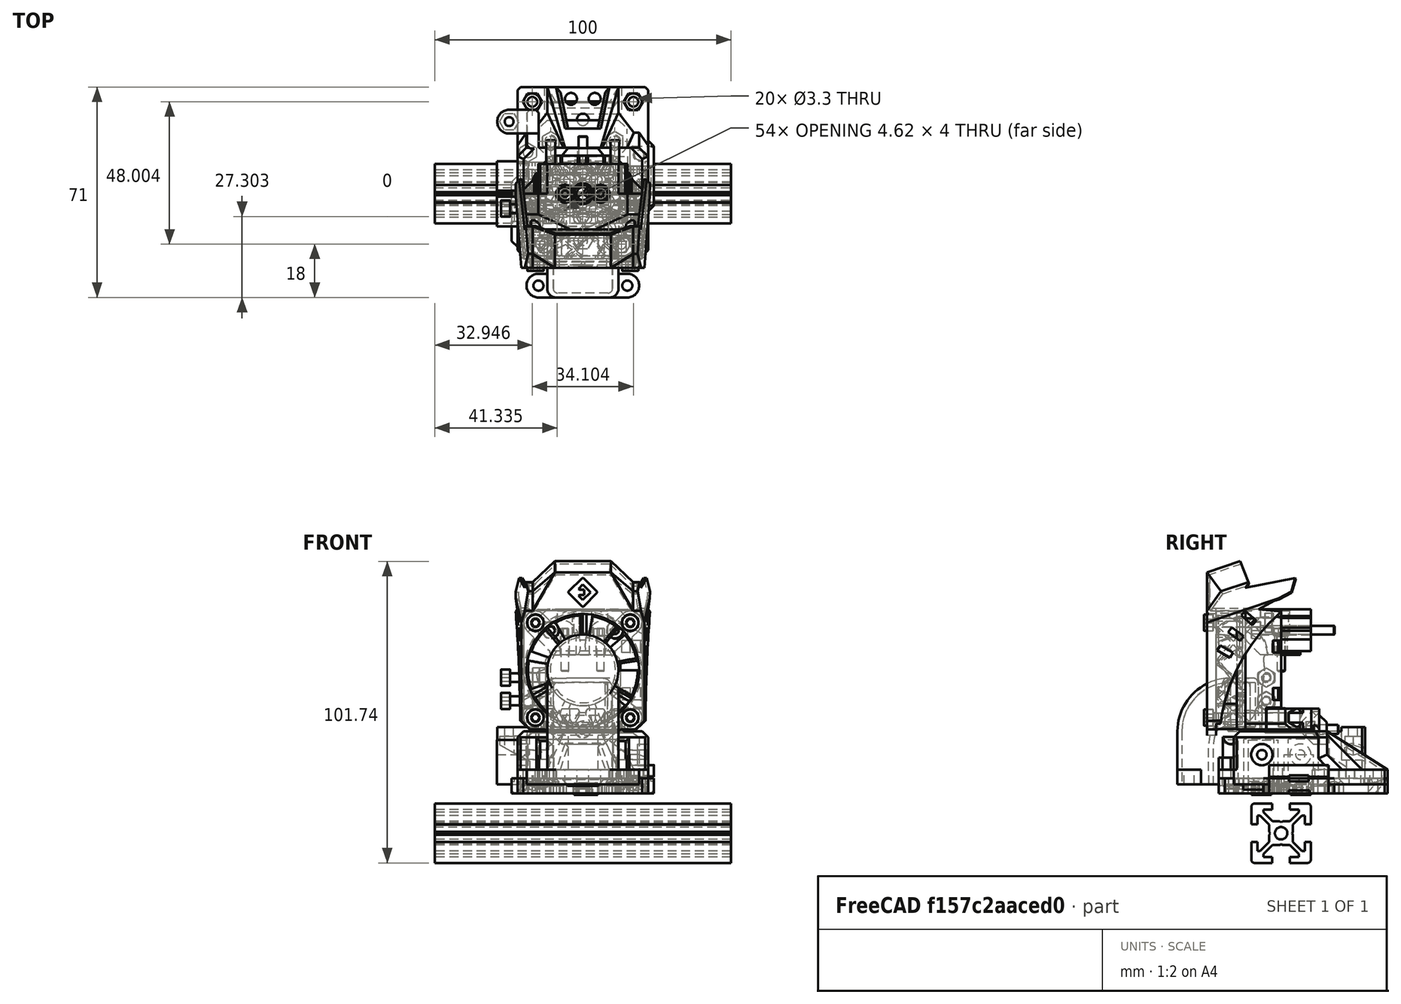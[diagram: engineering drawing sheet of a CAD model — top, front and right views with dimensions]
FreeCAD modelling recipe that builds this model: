
FCSTD DOCUMENT  (FreeCAD 0.19R24291 (Git))
Label: face-plate
License: Other
LicenseURL: GPL3
objects: Part::Feature×62, Part::MultiFuse×19, Part::Box×18, Part::Cylinder×16, Part::Cut×14, Part::Chamfer×6, Part::Refine×3, Part::Fillet×3, App::Part×2, Part::Extrusion×1, Part::MultiCommon×1
note: 143 computed .brp shape members not serialized (recipe doc carries the construction recipe); baked Part::Feature solids carry a one-line shape summary decoded from their .brp

FEATURE [Part::Cylinder] Cylinder
  Angle = 360
  AttacherType = Attacher::AttachEngine3D
  Height = 10
  Placement = pos=(-10.8,17.71,0) rot=(0,0,1;1.5708rad)
  Radius = 2
FEATURE [Part::Cylinder] Cylinder001
  Angle = 360
  AttacherType = Attacher::AttachEngine3D
  Height = 10
  Placement = pos=(10.8,17.705,0) rot=(0,0,1;0rad)
  Radius = 2
FEATURE [Part::MultiFuse] Fusion002
  Shapes = -> [Cylinder001,Cylinder]
FEATURE [Part::Feature] Extrude003002001  label="2020"
  Placement = pos=(50,0,-13) rot=(0,-1,0;1.5708rad)
  shape: bbox 100 x 20 x 20 mm, 63 faces (baked)
FEATURE [Part::Box] Box004  label="Cube004"
  AttacherType = Attacher::AttachEngine3D
  Height = 10.39
  Length = 2.5
  Placement = pos=(12.5,2.75,0) rot=(0,0,1;0rad)
  Width = 6.5
FEATURE [Part::Box] Box005  label="Cube005"
  AttacherType = Attacher::AttachEngine3D
  Height = 10.39
  Length = 2.5
  Placement = pos=(-15,-9.25,0) rot=(0,0,1;0rad)
  Width = 6.5
FEATURE [Part::Box] Box006  label="Cube006"
  AttacherType = Attacher::AttachEngine3D
  Height = 2.5
  Length = 10
  Placement = pos=(-37,-9.5,-1) rot=(0,0,1;0rad)
  Width = 7
FEATURE [Part::Box] Box007  label="Cube007"
  AttacherType = Attacher::AttachEngine3D
  Height = 2.5
  Length = 10
  Placement = pos=(28,2.5,-1) rot=(0,0,1;0rad)
  Width = 7
FEATURE [Part::Feature] Part__Feature008  label="mosquito005"
  Placement = pos=(-3.42e-14,-6.9e-14,18.5) rot=(0,0,1;0rad)
  shape: bbox 1.4 x 1.4 x 9.686 mm, 1 faces, 0 solids (baked)
FEATURE [Part::Feature] Part__Feature020  label="mosquito017"
  Placement = pos=(-3.42e-14,-6.9e-14,18.5) rot=(0,0,1;0rad)
  shape: bbox 7.8 x 7.8 x 0.4 mm, 3 faces, 0 solids (baked)
FEATURE [Part::Feature] Part__Feature021  label="mosquito018"
  Placement = pos=(-3.42e-14,-6.9e-14,18.5) rot=(0,0,1;0rad)
  shape: bbox 2 x 5.5 x 5.5 mm, 9 faces, 0 solids (baked)
FEATURE [Part::Feature] Part__Feature028  label="shroud"
  Placement = pos=(-2.78e-14,-25,42) rot=(0,0,1;0rad)
  shape: bbox 45.38 x 29.94 x 58.74 mm, 133 faces (baked)
FEATURE [Part::Feature] Part__Feature034  label="4010 FAN"
  Placement = pos=(-2.4e-14,-12,42) rot=(0,0,1;0rad)
  shape: bbox 40 x 10 x 40 mm, 104 faces (baked)
FEATURE [Part::Feature] Part__Feature017  label="mosquito014"
  Placement = pos=(-3.42e-14,-6.9e-14,18.5) rot=(0,0,1;0rad)
  shape: bbox 2.15 x 2.15 x 31.5 mm, 1 faces, 0 solids (baked)
FEATURE [Part::Feature] Part__Feature037  label="M3  Hex nut 002"
  Placement = pos=(16,-5.5,58) rot=(0.57735,-0.57735,-0.57735;4.18879rad)
  shape: bbox 7.805 x 2.436 x 7.805 mm, 21 faces (baked)
FEATURE [Part::Feature] Part__Feature039  label="M3  Hex nut 003"
  Placement = pos=(-16,-0.9,25.9843) rot=(0.57735,-0.57735,-0.57735;4.18879rad)
  shape: bbox 7.805 x 2.436 x 7.805 mm, 21 faces (baked)
FEATURE [Part::Feature] Part__Feature040  label="M3  Hex nut 004"
  Placement = pos=(-17,-5,39.5) rot=(0,1,0;1.5708rad)
  shape: bbox 2.436 x 7.805 x 7.805 mm, 21 faces (baked)
FEATURE [Part::Feature] Part__Feature018  label="mosquito015"
  Placement = pos=(-3.42e-14,-6.9e-14,18.5) rot=(0,0,1;0rad)
  shape: bbox 1.4 x 1.4 x 9.686 mm, 1 faces, 0 solids (baked)
FEATURE [Part::Feature] Part__Feature044  label="DIN 912 M2.5 12 mm001"
  Placement = pos=(6,0,53.6) rot=(1,0,0;3.14159rad)
  shape: bbox 5.066 x 5.066 x 14.5 mm, 15 faces (baked)
FEATURE [Part::Feature] Part__Feature032  label="M3  Hex nut 001"
  Placement = pos=(16,-0.9,26) rot=(0.57735,-0.57735,-0.57735;4.18879rad)
  shape: bbox 7.805 x 2.436 x 7.805 mm, 21 faces (baked)
FEATURE [Part::Feature] Part__Feature019  label="mosquito016"
  Placement = pos=(-3.42e-14,-6.9e-14,18.5) rot=(0,0,1;0rad)
  shape: bbox 2.16 x 2.16 x 14.5 mm, 1 faces, 0 solids (baked)
FEATURE [Part::Feature] Part__Feature015  label="mosquito012"
  Placement = pos=(-3.42e-14,-6.9e-14,18.5) rot=(0,0,1;0rad)
  shape: bbox 2.38 x 2.38 x 14.5 mm, 1 faces, 0 solids (baked)
FEATURE [Part::Feature] Part__Feature038  label="DIN 912 M2.5 12 mm"
  Placement = pos=(-6,0,53.6) rot=(1,0,0;3.14159rad)
  shape: bbox 5.066 x 5.066 x 14.5 mm, 15 faces (baked)
FEATURE [Part::Feature] Part__Feature029  label="DIN 912 M3 8 mm"
  Placement = pos=(0,11.35,22) rot=(0,0.707107,0.707107;3.14159rad)
  shape: bbox 5.953 x 11 x 5.953 mm, 15 faces (baked)
FEATURE [Part::Feature] Part__Feature041  label="mosquito_face"
  Placement = pos=(-2.78e-14,10,55.5) rot=(0,0,1;0rad)
  shape: bbox 40.01 x 24.77 x 40.61 mm, 124 faces (baked)
FEATURE [Part::Feature] Part__Feature042  label="DIN 912 M3 20 mm001"
  Placement = pos=(-16,-23,58) rot=(-1,0,0;1.5708rad)
  shape: bbox 5.953 x 23 x 5.953 mm, 15 faces (baked)
FEATURE [Part::Feature] Part__Feature030  label="DIN 912 M3 10 mm001"
  Placement = pos=(-24.6,-5.04159,31.6575) rot=(0.57735,-0.57735,0.57735;4.18879rad)
  shape: bbox 13 x 5.953 x 5.953 mm, 15 faces (baked)
FEATURE [Part::Feature] Part__Feature007  label="mosquito004"
  Placement = pos=(-3.42e-14,-6.9e-14,18.5) rot=(0,0,1;0rad)
  shape: bbox 23.27 x 18.01 x 12.51 mm, 54 faces, 0 solids (baked)
FEATURE [Part::Feature] Part__Feature013  label="mosquito010"
  Placement = pos=(-3.42e-14,-6.9e-14,18.5) rot=(0,0,1;0rad)
  shape: bbox 2 x 5.5 x 5.5 mm, 9 faces, 0 solids (baked)
FEATURE [Part::Feature] Part__Feature016  label="mosquito013"
  Placement = pos=(-3.42e-14,-6.9e-14,18.5) rot=(0,0,1;0rad)
  shape: bbox 6.2 x 6.2 x 7.765 mm, 5 faces, 0 solids (baked)
FEATURE [Part::Feature] Part__Feature009  label="mosquito006"
  Placement = pos=(-3.42e-14,-6.9e-14,18.5) rot=(0,0,1;0rad)
  shape: bbox 7.8 x 7.8 x 0.4 mm, 3 faces, 0 solids (baked)
FEATURE [Part::Feature] Part__Feature006  label="mosquito003"
  Placement = pos=(-3.42e-14,-6.9e-14,18.5) rot=(0,0,1;0rad)
  shape: bbox 9.503 x 9.503 x 1.942 mm, 13 faces, 0 solids (baked)
FEATURE [Part::Feature] Part__Feature001  label="DIN 912 M3 25 mm"
  Placement = pos=(10.8,-7,55.5) rot=(-1,0,0;1.5708rad)
  shape: bbox 5.953 x 28 x 5.953 mm, 15 faces (baked)
FEATURE [Part::Feature] Part__Feature011  label="mosquito008"
  Placement = pos=(-3.42e-14,-6.9e-14,18.5) rot=(0,0,1;0rad)
  shape: bbox 7 x 7 x 0.4 mm, 3 faces, 0 solids (baked)
FEATURE [Part::Feature] Part__Feature005  label="mosquito002"
  Placement = pos=(-3.42e-14,-6.9e-14,18.5) rot=(0,0,1;0rad)
  shape: bbox 25 x 13 x 25 mm, 187 faces, 0 solids (baked)
FEATURE [Part::Feature] Part__Feature014  label="mosquito011"
  Placement = pos=(-3.42e-14,-6.9e-14,18.5) rot=(0,0,1;0rad)
  shape: bbox 7.8 x 7.8 x 2.9 mm, 4 faces, 0 solids (baked)
FEATURE [Part::Feature] Part__Feature010  label="mosquito007"
  Placement = pos=(-3.42e-14,-6.9e-14,18.5) rot=(0,0,1;0rad)
  shape: bbox 2.16 x 2.16 x 14.5 mm, 1 faces, 0 solids (baked)
FEATURE [Part::Feature] Part__Feature035  label="DIN 912 M3 25 mm002"
  Placement = pos=(-10.8,-7,55.5) rot=(-1,0,0;1.5708rad)
  shape: bbox 5.953 x 28 x 5.953 mm, 15 faces (baked)
FEATURE [Part::Feature] Part__Feature002  label="DIN 912 M3 25 mm001"
  Placement = pos=(-16,-23,26) rot=(-1,0,0;1.5708rad)
  shape: bbox 5.953 x 28 x 5.953 mm, 15 faces (baked)
FEATURE [Part::Feature] Part__Feature  label="M3  Hex nut "
  Placement = pos=(-17,-5.04159,31.6575) rot=(0,1,0;1.5708rad)
  shape: bbox 2.436 x 7.805 x 7.805 mm, 21 faces (baked)
FEATURE [Part::Feature] Part__Feature004  label="mosquito001"
  Placement = pos=(-3.42e-14,-6.9e-14,18.5) rot=(0,0,1;0rad)
  shape: bbox 2.38 x 2.38 x 14.5 mm, 1 faces, 0 solids (baked)
FEATURE [Part::Feature] Part__Feature003  label="mosquito"
  Placement = pos=(-3.42e-14,-6.9e-14,18.5) rot=(0,0,1;0rad)
  shape: bbox 2.38 x 2.38 x 14.5 mm, 1 faces, 0 solids (baked)
FEATURE [Part::Feature] Part__Feature036  label="DIN 912 M3 25 mm003"
  Placement = pos=(16,-23,26) rot=(-1,0,0;1.5708rad)
  shape: bbox 5.953 x 28 x 5.953 mm, 15 faces (baked)
FEATURE [Part::Feature] Part__Feature012  label="mosquito009"
  Placement = pos=(-3.42e-14,-6.9e-14,18.5) rot=(0,0,1;0rad)
  shape: bbox 2.16 x 2.16 x 14.5 mm, 1 faces, 0 solids (baked)
FEATURE [Part::Feature] Part__Feature033  label="DIN 912 M3 20 mm"
  Placement = pos=(16,-23,58) rot=(-1,0,0;1.5708rad)
  shape: bbox 5.953 x 23 x 5.953 mm, 15 faces (baked)
FEATURE [Part::Feature] Part__Feature027  label="DIN 912 M3 10 mm"
  Placement = pos=(-24.6,-5,39.5) rot=(0.57735,-0.57735,0.57735;4.18879rad)
  shape: bbox 13 x 5.953 x 5.953 mm, 15 faces (baked)
FEATURE [Part::Feature] Part__Feature025  label="mosquito022"
  Placement = pos=(-3.42e-14,-6.9e-14,18.5) rot=(0,0,1;0rad)
  shape: bbox 2.16 x 2.16 x 14.5 mm, 1 faces, 0 solids (baked)
FEATURE [Part::Feature] Part__Feature026  label="mosquito023"
  Placement = pos=(-3.42e-14,-6.9e-14,18.5) rot=(0,0,1;0rad)
  shape: bbox 7.8 x 7.8 x 0.4 mm, 3 faces, 0 solids (baked)
FEATURE [Part::Feature] Part__Feature024  label="mosquito021"
  Placement = pos=(-3.42e-14,-6.9e-14,18.5) rot=(0,0,1;0rad)
  shape: bbox 7.002 x 7.002 x 12.16 mm, 22 faces, 0 solids (baked)
FEATURE [Part::Feature] Part__Feature023  label="mosquito020"
  Placement = pos=(-3.42e-14,-6.9e-14,18.5) rot=(0,0,1;0rad)
  shape: bbox 7.8 x 7.8 x 0.4 mm, 3 faces, 0 solids (baked)
FEATURE [Part::Feature] Part__Feature022  label="mosquito019"
  Placement = pos=(-3.42e-14,-6.9e-14,18.5) rot=(0,0,1;0rad)
  shape: bbox 2.38 x 2.38 x 14.5 mm, 1 faces, 0 solids (baked)
FEATURE [Part::Feature] Part__Feature043  label="M3  Hex nut 005"
  Placement = pos=(-16,-5.5,58) rot=(0.57735,-0.57735,-0.57735;4.18879rad)
  shape: bbox 7.805 x 2.436 x 7.805 mm, 21 faces (baked)
FEATURE [App::Part] mosquito__1_  label="mosquito <1>"
  Group = -> [Part__Feature003,Part__Feature004,Part__Feature005,Part__Feature006,Part__Feature007,Part__Feature008,Part__Feature009,Part__Feature010,Part__Feature011,Part__Feature012,Part__Feature013,Part__Feature014,Part__Feature015,Part__Feature016,Part__Feature017,Part__Feature018,Part__Feature019,Part__Feature020,Part__Feature021,Part__Feature022,Part__Feature023,Part__Feature024,Part__Feature025,+1 more]
  Origin = -> Origin
FEATURE [Part::Feature] Part__Feature031  label="mosquito_support"
  Placement = pos=(-2.78e-14,9.9,55.5) rot=(0,0,1;0rad)
  shape: bbox 40 x 20.25 x 12 mm, 97 faces (baked)
FEATURE [App::Part] _Face__Mosquito  label="[Face] Mosquito"
  Group = -> [Part__Feature,Part__Feature001,Part__Feature002,mosquito__1_,Part__Feature027,Part__Feature028,Part__Feature029,Part__Feature030,Part__Feature031,Part__Feature032,Part__Feature033,Part__Feature034,Part__Feature035,Part__Feature036,Part__Feature037,Part__Feature038,Part__Feature039,Part__Feature040,Part__Feature041,Part__Feature042,Part__Feature043,Part__Feature044]
  Origin = -> Origin001
  Placement = pos=(0,-38,18) rot=(1,0,0;4.71239rad)
FEATURE [Part::Feature] Fusion010  label="belt-teeth-cut001"
  Placement = pos=(-25,-6,4.5) rot=(0,0,1;0rad)
  shape: bbox 10 x 6.5 x 2.98 mm, 22 faces (baked)
FEATURE [Part::Feature] Fusion011  label="belt-teeth-cut002"
  Placement = pos=(25,6,4.5) rot=(0,0,1;3.14159rad)
  shape: bbox 10 x 6.5 x 2.98 mm, 22 faces (baked)
FEATURE [Part::MultiFuse] Fusion012
  Shapes = -> [Fusion011,Fusion010]
FEATURE [Part::Cylinder] Cylinder005
  Angle = 360
  AttacherType = Attacher::AttachEngine3D
  Height = 10
  Placement = pos=(19,13,0) rot=(0,0,1;0rad)
  Radius = 1.9
FEATURE [Part::Cylinder] Cylinder006
  Angle = 360
  AttacherType = Attacher::AttachEngine3D
  Height = 10
  Placement = pos=(-19,1,0) rot=(0,0,1;0rad)
  Radius = 1.9
FEATURE [Part::Cylinder] Cylinder007
  Angle = 360
  AttacherType = Attacher::AttachEngine3D
  Height = 10
  Placement = pos=(-19,-13,0) rot=(0,0,1;0rad)
  Radius = 1.9
FEATURE [Part::Cylinder] Cylinder008
  Angle = 360
  AttacherType = Attacher::AttachEngine3D
  Height = 10
  Placement = pos=(19,-1,0) rot=(0,0,1;0rad)
  Radius = 1.9
FEATURE [Part::Feature] Part__Feature074_cs001
  shape: bbox 30 x 14.2 x 3e-07 mm, 0 faces, 0 solids (baked)
FEATURE [Part::Feature] Body005  label="base-plate"
  shape: bbox 44.1 x 57 x 5 mm, 134 faces (baked)
FEATURE [Part::Extrusion] Extrude
  Base = -> Part__Feature074_cs001
  Dir = (0,0,1)
  DirMode = 2
  FaceMakerClass = Part::FaceMakerBullseye
  LengthFwd = 3
  LengthRev = 0
  Placement = pos=(0,0,-1) rot=(0,0,1;0rad)
  Solid = true
  Symmetric = false
FEATURE [Part::Feature] Part__Feature074  label="universal_face"
  Placement = pos=(-0.00422634,7.50353,0.50127) rot=(-1,0,0;1.5708rad)
  shape: bbox 44.11 x 57.01 x 8.01 mm, 258 faces (baked)
FEATURE [Part::MultiFuse] Fusion
  Shapes = -> [Extrude,Body005]
FEATURE [Part::Cut] Cut
  Base = -> Fusion
  Placement = pos=(0,0,0.5) rot=(0,0,1;0rad)
  Tool = -> Fusion002
FEATURE [Part::Feature] Body006  label="Body001"
  shape: bbox 5.6 x 5.6 x 10 mm, 3 faces (baked)
FEATURE [Part::Feature] Body007  label="Body002"
  Placement = pos=(26,0,0) rot=(0,0,1;0rad)
  shape: bbox 5.6 x 5.6 x 10 mm, 3 faces (baked)
FEATURE [Part::MultiFuse] Fusion015
  Placement = pos=(0,0,3) rot=(0,0,1;0rad)
  Shapes = -> [Body007,Body006]
FEATURE [Part::Box] Box  label="Cube"
  AttacherType = Attacher::AttachEngine3D
  Height = 10
  Length = 15
  Placement = pos=(-7.5,-21,2.5) rot=(0,0,1;0rad)
  Width = 11
FEATURE [Part::Feature] Part__Feature075  label="universal_face001"
  Placement = pos=(-0.00422634,7.50353,0.50127) rot=(-1,0,0;1.5708rad)
  shape: bbox 44.11 x 57.01 x 8.01 mm, 258 faces (baked)
FEATURE [Part::Cut] Cut006
  Base = -> Box
  Tool = -> Part__Feature075
FEATURE [Part::Cylinder] Cylinder009
  Angle = 360
  AttacherType = Attacher::AttachEngine3D
  Height = 1
  Placement = pos=(0,-15.8,2) rot=(0,0,1;0rad)
  Radius = 4
FEATURE [Part::Cylinder] Cylinder010
  Angle = 360
  AttacherType = Attacher::AttachEngine3D
  Height = 1
  Placement = pos=(0,-15.8,2) rot=(0,0,1;0rad)
  Radius = 1.65
FEATURE [Part::Cylinder] Cylinder011
  Angle = 360
  AttacherType = Attacher::AttachEngine3D
  Height = 10
  Placement = pos=(0,7,0) rot=(0,0,1;0rad)
  Radius = 1.6
FEATURE [Part::Cylinder] Cylinder012
  Angle = 360
  AttacherType = Attacher::AttachEngine3D
  Height = 10
  Placement = pos=(0,-7,0) rot=(0,0,1;0rad)
  Radius = 1.6
FEATURE [Part::Box] Box008  label="Cube008"
  AttacherType = Attacher::AttachEngine3D
  Height = 4
  Length = 8
  Placement = pos=(-3,-10,0) rot=(0,0,1;0rad)
  Width = 20
FEATURE [Part::MultiFuse] Fusion017
  Shapes = -> [Cylinder011,Cylinder012]
FEATURE [Part::Box] Box009  label="Cube009"
  AttacherType = Attacher::AttachEngine3D
  Height = 0.5
  Length = 10
  Placement = pos=(-4,-3.25,0) rot=(0,0,1;0rad)
  Width = 6.5
FEATURE [Part::Feature] Cut008004001  label="back-body-plain"
  Placement = pos=(0,0,3.5) rot=(0,0,1;0rad)
  shape: bbox 50.93 x 72.49 x 37.34 mm, 290 faces (baked)
FEATURE [Part::Cylinder] Cylinder013
  Angle = 360
  AttacherType = Attacher::AttachEngine3D
  Height = 44
  Placement = pos=(21.5,6.5,13.5) rot=(0.707107,0,-0.707107;3.14159rad)
  Radius = 1.6
FEATURE [Part::Cylinder] Cylinder014
  Angle = 360
  AttacherType = Attacher::AttachEngine3D
  Height = 44
  Placement = pos=(-21.5,-6.5,13.5) rot=(0,1,0;1.5708rad)
  Radius = 1.6
FEATURE [Part::Cylinder] Cylinder015
  Angle = 360
  AttacherType = Attacher::AttachEngine3D
  Height = 4
  Placement = pos=(18.5,-6.5,13.5) rot=(0,1,0;1.5708rad)
  Radius = 3.6
FEATURE [Part::Cylinder] Cylinder016
  Angle = 360
  AttacherType = Attacher::AttachEngine3D
  Height = 4
  Placement = pos=(-18.5,6.5,13.5) rot=(0.707107,0,-0.707107;3.14159rad)
  Radius = 3.6
FEATURE [Part::Box] Box012  label="belt-slot"
  AttacherType = Attacher::AttachEngine3D
  Height = 10.2
  Length = 27
  Placement = pos=(-12,12.6,3.5) rot=(1,0,0;1.5708rad)
  Width = 15.2
FEATURE [Part::Box] Box013  label="belt-slot003"
  AttacherType = Attacher::AttachEngine3D
  Height = 10.2
  Length = 27
  Placement = pos=(-15,-2.4,3.5) rot=(1,0,0;1.5708rad)
  Width = 15.2
FEATURE [Part::MultiFuse] Fusion001007010
  Shapes = -> [Cylinder015,Cylinder016,Cylinder013,Cylinder014]
FEATURE [Part::Feature] Cut008003001  label="belt-clamp001"
  shape: bbox 6 x 20 x 4 mm, 16 faces (baked)
FEATURE [Part::Box] Box014  label="Cube012"
  AttacherType = Attacher::AttachEngine3D
  Height = 10
  Length = 26
  Placement = pos=(-13,27,0) rot=(0,0,1;0rad)
  Width = 10
FEATURE [Part::Feature] Fusion001007011001  label="face-plate-merged001"
  shape: bbox 44.1 x 57 x 8 mm, 220 faces (baked)
FEATURE [Part::Box] Box010  label="Cube010"
  AttacherType = Attacher::AttachEngine3D
  Height = 10
  Length = 10
  Placement = pos=(-29,1,3.5) rot=(0,0,1;0rad)
  Width = 10
FEATURE [Part::Box] Box011  label="Cube011"
  AttacherType = Attacher::AttachEngine3D
  Height = 15
  Length = 10
  Placement = pos=(-29,-11,3.5) rot=(0,0,1;0rad)
  Width = 10
FEATURE [Part::Box] Box016  label="Cube014"
  AttacherType = Attacher::AttachEngine3D
  Height = 2
  Length = 10
  Placement = pos=(-43.5,-11,2.5) rot=(0,0,1;0rad)
  Width = 10
FEATURE [Part::Box] Box017  label="Cube015"
  AttacherType = Attacher::AttachEngine3D
  Height = 2
  Length = 10
  Placement = pos=(25,1,2.5) rot=(0,0,1;0rad)
  Width = 10
FEATURE [Part::Chamfer] Chamfer001
  Base = -> Box016
  Edges = 1 edges r=1: [Edge6]
  Placement = pos=(12.45,0,0) rot=(0,0,1;0rad)
FEATURE [Part::Chamfer] Chamfer002
  Base = -> Box017
  Edges = 1 edges r=1: [Edge2]
  Placement = pos=(-3.95,0,0) rot=(0,0,1;0rad)
FEATURE [Part::MultiFuse] Fusion001007011002
  Shapes = -> [Chamfer002,Chamfer001]
FEATURE [Part::MultiFuse] Fusion001007011004
  Shapes = -> [Box005,Box004]
FEATURE [Part::Chamfer] Chamfer003
  Base = -> Box006
  Edges = 1 edges r=1: [Edge6]
  Placement = pos=(3.95,0,0) rot=(0,0,1;0rad)
FEATURE [Part::Chamfer] Chamfer004
  Base = -> Box007
  Edges = 1 edges r=1: [Edge2]
  Placement = pos=(-4.95,0,0) rot=(0,0,1;0rad)
FEATURE [Part::MultiFuse] Fusion001007011006
  Shapes = -> [Fusion012,Fusion001007011004]
FEATURE [Part::Cut] Cut008004003010
  Base = -> Cylinder009
  Tool = -> Cylinder010
FEATURE [Part::Feature] Part__Feature076  label="universal_face002"
  Placement = pos=(-0.00422634,7.50353,0.50127) rot=(-1,0,0;1.5708rad)
  shape: bbox 44.11 x 57.01 x 8.01 mm, 258 faces (baked)
FEATURE [Part::MultiCommon] Common
  Placement = pos=(0,0,-0.00126953) rot=(0,0,1;0rad)
  Shapes = -> [Part__Feature076,Box014]
FEATURE [Part::Box] Box018  label="Cube016"
  AttacherType = Attacher::AttachEngine3D
  Height = 10
  Length = 26
  Placement = pos=(-13,27,0) rot=(0,0,1;0rad)
  Width = 10
FEATURE [Part::Cylinder] Cylinder017
  Angle = 360
  AttacherType = Attacher::AttachEngine3D
  Height = 10
  Placement = pos=(17.05,31,3.5) rot=(0,0,1;1.5708rad)
  Radius = 3
FEATURE [Part::Cylinder] Cylinder018
  Angle = 360
  AttacherType = Attacher::AttachEngine3D
  Height = 10
  Placement = pos=(-17.05,31,3.5) rot=(0,0,1;1.5708rad)
  Radius = 3
FEATURE [Part::MultiFuse] Fusion001007011011
  Shapes = -> [Cylinder018,Cylinder017]
FEATURE [Part::Feature] Frantic_Trug_1_001001_solid  label="snakeoil-logo"
  Placement = pos=(13,-13.5,20.85) rot=(0,0,1;0rad)
  shape: bbox 37 x 22 x 4 mm, 291 faces (baked)
FEATURE [Part::MultiFuse] Fusion001007011012
  Shapes = -> [Box012,Box013]
FEATURE [Part::MultiFuse] Fusion001007011013
  Shapes = -> [Fusion001007010,Fusion001007011012,Fusion001007011002]
FEATURE [Part::Cut] Cut008004003012001002
  Base = -> Cut008004001
  Tool = -> Fusion001007011013
FEATURE [Part::Box] Box019  label="Cube017"
  AttacherType = Attacher::AttachEngine3D
  Height = 0.5
  Length = 24
  Placement = pos=(-11,-4,20.85) rot=(0,0,1;0rad)
  Width = 17
FEATURE [Part::MultiFuse] Fusion001007011014
  Shapes = -> [Cut008004003012001002,Box019]
FEATURE [Part::Cut] Cut008004003012001003
  Base = -> Fusion001007011014
  Tool = -> Frantic_Trug_1_001001_solid
FEATURE [Part::Refine] Cut008004003012001003001
  Source = -> Cut008004003012001003
FEATURE [Part::Feature] Cut008004003012001003001001
  shape: bbox 50.93 x 72.49 x 37.34 mm, 488 faces (baked)
FEATURE [Part::Box] Box020  label="Cube018"
  AttacherType = Attacher::AttachEngine3D
  Height = 5
  Length = 3
  Placement = pos=(21,-6,0.5) rot=(0,0,1;0rad)
  Width = 24
FEATURE [Part::Box] Box021  label="Cube019"
  AttacherType = Attacher::AttachEngine3D
  Height = 5
  Length = 3
  Placement = pos=(-24,-18,0.5) rot=(0,0,1;0rad)
  Width = 24
FEATURE [Part::Chamfer] Chamfer005
  Base = -> Box021
  Edges = 2 edges r=2: [Edge1,Edge3]
FEATURE [Part::Chamfer] Chamfer006
  Base = -> Box020
  Edges = 2 edges r=2: [Edge5,Edge7]
FEATURE [Part::MultiFuse] Fusion001007011015
  Shapes = -> [Chamfer005,Chamfer006]
FEATURE [Part::MultiFuse] Fusion001007011016
  Shapes = -> [Cut,Fusion001007011015]
FEATURE [Part::MultiFuse] Fusion001007011017
  Shapes = -> [Chamfer004,Chamfer003]
FEATURE [Part::Cut] Cut008004003012001003001002
  Base = -> Fusion001007011016
  Tool = -> Fusion001007011017
FEATURE [Part::Cut] Cut008004003012001003001003
  Base = -> Cut008004003012001003001002
  Tool = -> Fusion015
FEATURE [Part::MultiFuse] Fusion001007011018
  Shapes = -> [Cylinder006,Cylinder005,Cylinder007,Cylinder008]
FEATURE [Part::Cut] Cut008004003012001003001004
  Base = -> Cut008004003012001003001003
  Tool = -> Fusion001007011018
FEATURE [Part::Cut] Cut008004003012001003001005
  Base = -> Cut008004003012001003001004
  Tool = -> Fusion001007011006
FEATURE [Part::Cut] Cut008004003012001003001006
  Base = -> Cut008004003012001003001005
  Tool = -> Cut006
FEATURE [Part::Cut] Cut008004003012001003001007
  Base = -> Cut008004003012001003001006
  Tool = -> Fusion001007011011
FEATURE [Part::Cut] Cut008004003012001003001008
  Base = -> Cut008004003012001003001007
  Tool = -> Box018
FEATURE [Part::MultiFuse] Fusion001007011019
  Shapes = -> [Common,Cut008004003012001003001008]
FEATURE [Part::MultiFuse] Fusion001007011020
  Shapes = -> [Cut008004003010,Fusion001007011019]
FEATURE [Part::Fillet] Fillet
  Base = -> Fusion001007011020
  Edges = 2 edges r=2: [Edge253,Edge300]
FEATURE [Part::Fillet] Fillet001  label="face-plate-rf"
  Base = -> Fillet
  Edges = 2 edges r=1: [Edge471,Edge603]
FEATURE [Part::Fillet] Fillet002
  Base = -> Box008
  Edges = 4 edges r=1: [Edge1,Edge3,Edge5,Edge7]
FEATURE [Part::Cut] Cut008004003012001003001009
  Base = -> Fillet002
  Tool = -> Fusion017
FEATURE [Part::Cut] Cut008004003012001003001010  label="belt-clamp"
  Base = -> Cut008004003012001003001009
  Tool = -> Box009
FEATURE [Part::Refine] Fillet001001  label="face-plate-rf001"
  Source = -> Fillet001
FEATURE [Part::Refine] Cut008004003012001003001010001  label="belt-clamp002"
  Source = -> Cut008004003012001003001010
FEATURE [Part::Feature] Fillet001001001  label="face-plate-rf002"
  shape: bbox 48 x 57 x 8 mm, 236 faces (baked)
FEATURE [Part::Feature] Cut008004003012001003001010001001  label="belt-clamp003"
  Placement = pos=(19,6,6) rot=(0,0,1;0rad)
  shape: bbox 8 x 20 x 4 mm, 16 faces (baked)
